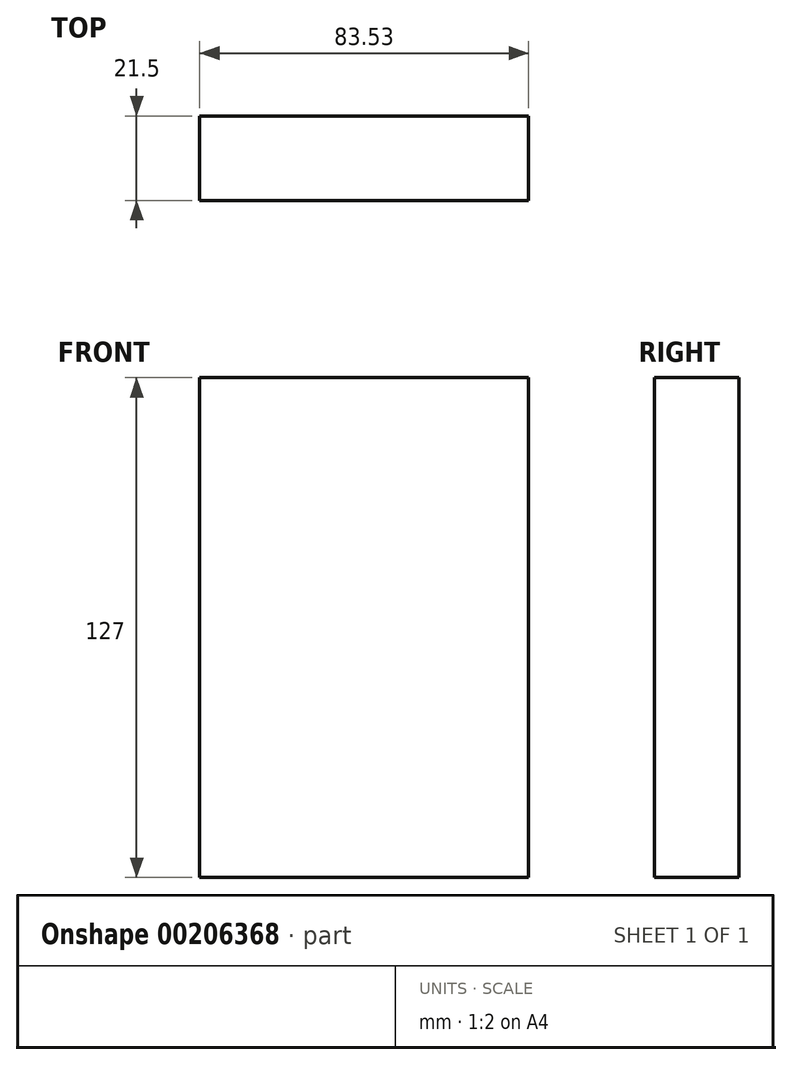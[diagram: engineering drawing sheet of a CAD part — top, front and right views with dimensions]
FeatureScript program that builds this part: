
annotation { "Feature Type Name" : "Feature", "Feature Type Description" : "" }
export const myFeature = defineFeature(function(context is Context, id is Id, definition is map)
    precondition{}
    {
        {
            var Q0;
            Q0=qCreatedBy(makeId("Top.planeOp"),FACE);
            var sketch = newSketch(context, id + "F0", { "sketchPlane" : qUnion([Q0])});
            skLineSegment(sketch, "E0.bottom", {"start": v(-40.15, 8.66) * mm, "end": v(43.38, 8.66) * mm});
            skLineSegment(sketch, "E0.top", {"start": v(-40.15, -12.84) * mm, "end": v(43.38, -12.84) * mm});
            skLineSegment(sketch, "E0.left", {"start": v(-40.15, 8.66) * mm, "end": v(-40.15, -12.84) * mm});
            skLineSegment(sketch, "E0.right", {"start": v(43.38, 8.66) * mm, "end": v(43.38, -12.84) * mm});
            skSolve(sketch);
        }
        {
            var Q0;
            Q0=makeQuery(id+"F0.imprint","IMPRINT",FACE,{"disambiguationData":[TD([[makeQuery(id+"F0.imprint","IMPRINT",EDGE,{"derivedFrom":sQuery(id+"F0.wireOp",EDGE,"E0.bottom")}),-1.0]])]});
            extrude(context, id + "F1", {"entities" : qUnion([Q0]), "endBound" : BoundingType.SYMMETRIC, "depth" : 127 * mm});
        }
    });
